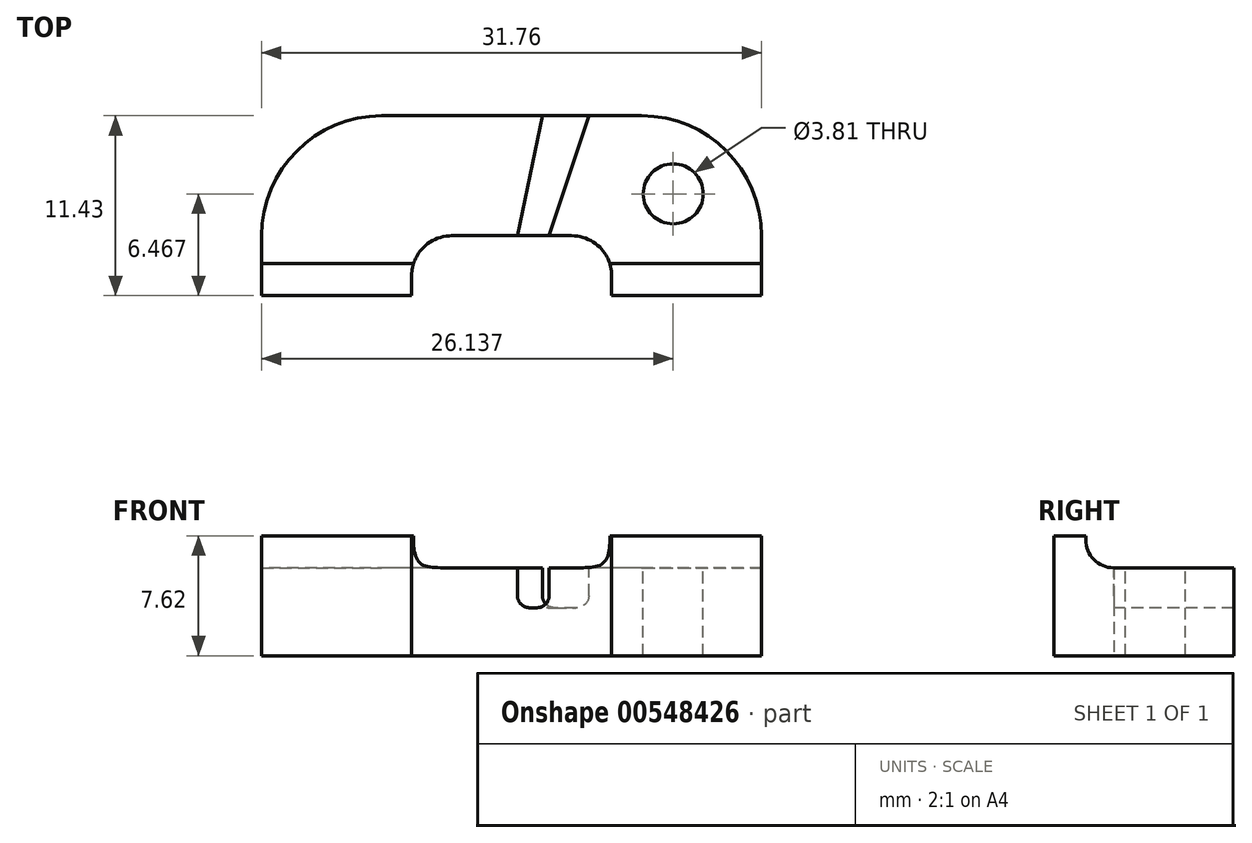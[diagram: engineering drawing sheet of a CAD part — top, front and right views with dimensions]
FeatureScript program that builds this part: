
annotation { "Feature Type Name" : "Feature", "Feature Type Description" : "" }
export const myFeature = defineFeature(function(context is Context, id is Id, definition is map)
    precondition{}
    {
        {
            var Q0;
            Q0=qCreatedBy(makeId("Top.planeOp"),FACE);
            var sketch = newSketch(context, id + "F0", { "sketchPlane" : qUnion([Q0])});
            skLineSegment(sketch, "E0", {"start": v(-3.8, 5.08) * mm, "end": v(3.81, 5.08) * mm});
            skLineSegment(sketch, "E1", {"start": v(-6.35, 1.27) * mm, "end": v(-15.88, 1.27) * mm});
            skLineSegment(sketch, "E2", {"start": v(6.35, 1.27) * mm, "end": v(15.88, 1.27) * mm});
            skLineSegment(sketch, "E3", {"start": v(-6.35, 1.27) * mm, "end": v(-6.35, 2.54) * mm});
            skLineSegment(sketch, "E4", {"start": v(6.35, 1.27) * mm, "end": v(6.35, 2.54) * mm});
            skLineSegment(sketch, "E5", {"start": v(-15.87, 1.27) * mm, "end": v(-15.87, 5.08) * mm});
            skLineSegment(sketch, "E6", {"start": v(15.88, 1.27) * mm, "end": v(15.88, 5.08) * mm});
            skPoint(sketch, "E7.visualSharp", {"position": v(-6.35, 5.08) * mm});
            skArc(sketch, "E7.filletArc", {"start": v(-3.8, 5.08) * mm, "mid": v(-5.6, 4.34) * mm, "end": v(-6.35, 2.54) * mm});
            skPoint(sketch, "E8.visualSharp", {"position": v(6.35, 5.08) * mm});
            skArc(sketch, "E8.filletArc", {"start": v(6.35, 2.54) * mm, "mid": v(5.6, 4.34) * mm, "end": v(3.81, 5.08) * mm});
            skArc(sketch, "E9.filletArc", {"start": v(-8.25, 12.7) * mm, "mid": v(-13.64, 10.47) * mm, "end": v(-15.87, 5.08) * mm});
            skArc(sketch, "E10.filletArc", {"start": v(15.88, 5.08) * mm, "mid": v(13.64, 10.47) * mm, "end": v(8.25, 12.7) * mm});
            skLineSegment(sketch, "E11", {"start": v(-8.25, 12.7) * mm, "end": v(8.25, 12.7) * mm});
            skSolve(sketch);
        }
        {
            var Q0;
            Q0 = qSketchRegion(id + "F0", true);
            extrude(context, id + "F1", {"entities" : qUnion([Q0]), "depth" : 7.62 * mm, "offsetDistance" : 25.4 * mm});
        }
        {
            var Q0;
            Q0=makeQuery(id+"F1.opExtrude","CAP_FACE",FACE,{"disambiguationData":[OSD([sQuery(id+"F0.wireOp",EDGE,"E0"),sQuery(id+"F0.wireOp",EDGE,"E1"),sQuery(id+"F0.wireOp",EDGE,"E2"),sQuery(id+"F0.wireOp",EDGE,"E3"),sQuery(id+"F0.wireOp",EDGE,"E4"),sQuery(id+"F0.wireOp",EDGE,"E5"),sQuery(id+"F0.wireOp",EDGE,"E6"),sQuery(id+"F0.wireOp",EDGE,"E7.filletArc"),sQuery(id+"F0.wireOp",EDGE,"E8.filletArc"),sQuery(id+"F0.wireOp",EDGE,"lg1CUv7w-emMP-6I0M-IDU1-Bxlh0eeama35"),sQuery(id+"F0.wireOp",EDGE,"E9.filletArc"),sQuery(id+"F0.wireOp",EDGE,"E10.filletArc")])],"isStart":false});
            var sketch = newSketch(context, id + "F2", { "sketchPlane" : qUnion([Q0])});
            skLineSegment(sketch, "E12", {"start": v(0, 0) * mm, "end": v(6.32, 23.58) * mm, "construction": true});
            skLineSegment(sketch, "E13", {"start": v(0.35, 5) * mm, "end": v(2.15, 13.68) * mm});
            skLineSegment(sketch, "E14", {"start": v(4.97, 12.92) * mm, "end": v(2.2, 4.5) * mm});
            skLineSegment(sketch, "E15", {"start": v(0.35, 5) * mm, "end": v(2.2, 4.5) * mm});
            skLineSegment(sketch, "E16", {"start": v(2.15, 13.68) * mm, "end": v(4.97, 12.92) * mm});
            skSolve(sketch);
        }
        {
            var Q0;
            Q0 = qSketchRegion(id + "F2", true);
            extrude(context, id + "F3", {"entities" : qUnion([Q0]), "operationType" : NewBodyOperationType.REMOVE, "oppositeDirection" : true, "depth" : 4.57 * mm, "offsetDistance" : 25.4 * mm});
        }
        {
            var Q0;
            Q0=makeQuery(id+"FFcCvfIx8KBxbnt_1.boolean.opBoolean","COPY",EDGE,{"derivedFrom":makeQuery(id+"FFcCvfIx8KBxbnt_1.opExtrude","CAP_EDGE",EDGE,{"disambiguationData":[OSD([sQuery(id+"FkL8yOZcJLCg7Uw_1.wireOp",EDGE,"rb6KwfnE-XR4J-STc7-UG4T-IN6j3M8JkOAb")])],"isStart":false})});
            var Q1;
            Q1=makeQuery(id+"F3.boolean.opBoolean","COPY",EDGE,{"derivedFrom":makeQuery(id+"F3.opExtrude","CAP_EDGE",EDGE,{"disambiguationData":[OSD([sQuery(id+"F2.wireOp",EDGE,"E13")])],"isStart":false})});
            var Q2;
            Q2=makeQuery(id+"F3.boolean.opBoolean","COPY",EDGE,{"derivedFrom":makeQuery(id+"F3.opExtrude","CAP_EDGE",EDGE,{"disambiguationData":[OSD([sQuery(id+"F2.wireOp",EDGE,"E14")])],"isStart":false})});
            fillet(context, id + "F4", {"entities" : qUnion([Q0, Q1, Q2]), "radius" : 0.76 * mm, "tangentPropagation" : true, "allowEdgeOverflow" : false});
        }
        {
            var Q0;
            {var subQ0=sQuery(id+"F0.wireOp",EDGE,"E6");var subQ1=sQuery(id+"F0.wireOp",EDGE,"E4");var subQ2=sQuery(id+"F0.wireOp",EDGE,"E2");var subQ3=sQuery(id+"F0.wireOp",EDGE,"E0");var subQ4=sQuery(id+"F0.wireOp",EDGE,"E8.filletArc");var subQ5=sQuery(id+"F0.wireOp",EDGE,"E10.filletArc");var subQ6=sQuery(id+"F0.wireOp",EDGE,"7SGZqKLD-pBsY-eMjj-JAuF-ZC1RzZtCAISt");Q0=makeQuery(id+"F3.boolean.opBoolean","SPLIT",FACE,{"disambiguationData":[TD([makeQuery(id+"F1.opExtrude","SWEPT_FACE",FACE,{"disambiguationData":[OSD([subQ2])]})])],"derivedFrom":makeQuery(id+"F1.opExtrude","CAP_FACE",FACE,{"disambiguationData":[OSD([subQ3,sQuery(id+"F0.wireOp",EDGE,"E1"),subQ2,sQuery(id+"F0.wireOp",EDGE,"E3"),subQ1,sQuery(id+"F0.wireOp",EDGE,"E5"),subQ0,sQuery(id+"F0.wireOp",EDGE,"E7.filletArc"),subQ4,sQuery(id+"F0.wireOp",EDGE,"E9.filletArc"),subQ5,subQ6])],"isStart":false})});}
            var sketch = newSketch(context, id + "F5", { "sketchPlane" : qUnion([Q0])});
            skCircle(sketch, "E17", {"center": v(10.26, 7.74) * mm, "radius": 1.9 * mm});
            skSolve(sketch);
        }
        {
            var Q0;
            Q0 = qSketchRegion(id + "F5", true);
            extrude(context, id + "F6", {"entities" : qUnion([Q0]), "operationType" : NewBodyOperationType.REMOVE, "endBound" : BoundingType.THROUGH_ALL, "oppositeDirection" : true, "depth" : 25.4 * mm, "offsetDistance" : 25.4 * mm});
        }
        {
            var Q0;
            Q0=makeQuery(id+"F1.opExtrude","SWEPT_FACE",FACE,{"disambiguationData":[OSD([sQuery(id+"F0.wireOp",EDGE,"E5")])]});
            var sketch = newSketch(context, id + "F7", { "sketchPlane" : qUnion([Q0])});
            skLineSegment(sketch, "E18.bottom", {"start": v(-12.7, 7.62) * mm, "end": v(-3.3, 7.62) * mm});
            skLineSegment(sketch, "E18.top", {"start": v(-12.7, 5.59) * mm, "end": v(-5.08, 5.59) * mm});
            skLineSegment(sketch, "E18.left", {"start": v(-12.7, 7.62) * mm, "end": v(-12.7, 5.59) * mm});
            skLineSegment(sketch, "E18.right", {"start": v(-3.3, 7.62) * mm, "end": v(-3.3, 7.37) * mm});
            skPoint(sketch, "E19.visualSharp", {"position": v(-3.3, 5.59) * mm});
            skArc(sketch, "E19.filletArc", {"start": v(-5.08, 5.59) * mm, "mid": v(-3.82, 6.1) * mm, "end": v(-3.3, 7.37) * mm});
            skSolve(sketch);
        }
        {
            var Q0;
            Q0 = qSketchRegion(id + "F7", true);
            extrude(context, id + "F8", {"entities" : qUnion([Q0]), "operationType" : NewBodyOperationType.REMOVE, "endBound" : BoundingType.THROUGH_ALL, "oppositeDirection" : true, "depth" : 25.4 * mm, "offsetDistance" : 25.4 * mm});
        }
    });
